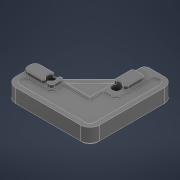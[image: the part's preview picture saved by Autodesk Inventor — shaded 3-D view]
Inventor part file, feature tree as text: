
AUTODESK INVENTOR PART (.ipt)
format: ipt  version: 2022.1 (Build 261234020, 234B)  size: 1,088,512 bytes
history: native  units: mm
features: projected_geometry x18, move_body x16, direct_edit x14, fillet x13, extrude x12, sketch x11, delete_face x9, chamfer x4, plane x1, other x1
ambient origin geometry x8: Origin, YZ Plane, XZ Plane, XY Plane, X Axis, Y Axis, Z Axis, Center Point
bodies: Volumenkörper1 (feature_tree)
feature tree (99):
  direct_edit  "Direktbearbeitung1"
  direct_edit  "Direktbearbeitung2"
  delete_face  "Fläche löschen1"
  extrude  "Extrusion1"  Depth=5.4mm TaperAngle=0.0deg
  fillet  "Rundung1"  Radius=0.5mm
  fillet  "Rundung2"  Radius=6.0mm
  extrude  "Extrusion2"  Depth=1.0mm
  fillet  "Rundung3"  Radius=1.0mm
  extrude  "Extrusion3"  Depth=2.0mm
  delete_face  "Fläche löschen2"
  extrude  "Extrusion4"  Depth=20.0mm
  direct_edit  "Direktbearbeitung3"
  extrude  "Extrusion5"  Depth=1.0mm
  chamfer  "Fase3"  Distance=0.2mm
  plane  "Arbeitsebene1"
  extrude  "Extrusion6"  Depth=0.6mm TaperAngle=0.0deg
  direct_edit  "Direktbearbeitung4"
  direct_edit  "Direktbearbeitung5"
  chamfer  "Fase5"  [1 undecoded]
  direct_edit  "Direktbearbeitung6"
  chamfer  "Fase6"  Distance=1.6mm
  direct_edit  "Direktbearbeitung8"
  delete_face  "Fläche löschen4"
  direct_edit  "Direktbearbeitung9"
  fillet  "Rundung4"  Radius=0.2mm
  fillet  "Rundung5"  Radius=2.0mm
  fillet  "Rundung6"  Radius=16.4mm
  delete_face  "Fläche löschen5"
  delete_face  "Fläche löschen6"
  extrude  "Extrusion7"  Depth=0.6mm
  fillet  "Rundung7"  Radius=0.8mm
  direct_edit  "Direktbearbeitung10"
  sketch  "Skizze8"  dims[d22=1.0mm]
  extrude  "Extrusion8"  Depth=0.6mm
  extrude  "Extrusion9"  Depth=0.6mm
  chamfer  "Fase7"  Distance=0.8mm
  direct_edit  "Direktbearbeitung11"
  extrude  "Extrusion10"  Depth=0.6mm
  fillet  "Rundung8"  Radius=0.4mm
  direct_edit  "Direktbearbeitung12"
  direct_edit  "Direktbearbeitung13"
  fillet  "Rundung9"  Radius=0.4mm
  direct_edit  "Direktbearbeitung14"
  delete_face  "Fläche löschen7"
  delete_face  "Fläche löschen8"
  delete_face  "Fläche löschen9"
  delete_face  "Fläche löschen10"
  direct_edit  "Direktbearbeitung15"
  extrude  "Extrusion11"  Depth=3.0mm
  fillet  "Rundung10"  Radius=3.8mm
  extrude  "Extrusion12"  Depth=0.6mm TaperAngle=0.0deg
  fillet  "Rundung11"  Radius=18.4mm
  fillet  "Rundung12"  Radius=0.6mm
  fillet  "Rundung13"  [1 undecoded]
  sketch  "Skizze1"  dims[d0=0.0mm d1=0.0mm d2=1.4mm d3=0.0mm d4=0.0mm d5=5.4mm d6=0.5mm d7=6.0mm]
  projected_geometry  "Projizierte Kontur1"
  sketch  "Skizze2"  dims[d8=6.0mm d9=0.5mm d10=1.0mm d11=0.0mm]
  projected_geometry  "Projizierte Kontur2"
  projected_geometry  "Projizierte Kontur3"
  sketch  "Skizze3"  dims[d12=0.8mm d13=2.0mm]
  projected_geometry  "Projizierte Kontur4"
  sketch  "Skizze4"  dims[d14=20.0mm d15=20.0mm]
  projected_geometry  "Projizierte Kontur5"
  projected_geometry  "Projizierte Kontur6"
  sketch  "Skizze5"  dims[d16=1.0mm d17=0.0mm d18=1.0mm]
  projected_geometry  "Projizierte Kontur7"
  sketch  "Skizze6"  dims[d20=4.0mm]
  projected_geometry  "Projizierte Kontur8"
  sketch  "Skizze7"  dims[d21=4.0mm]
  projected_geometry  "Projizierte Kontur9"
  projected_geometry  "Projizierte Kontur10"
  projected_geometry  "Projizierte Kontur11"
  projected_geometry  "Projizierte Kontur12"
  projected_geometry  "Projizierte Kontur13"
  sketch  "Skizze9"  dims[d23=1.0mm]
  projected_geometry  "Projizierte Kontur14"
  projected_geometry  "Projizierte Kontur15"
  sketch  "Skizze10"  dims[d24=1.0mm]
  projected_geometry  "Projizierte Kontur16"
  sketch  "Skizze11"  dims[d25=1.0mm d26=0.2mm d27=0.0mm d28=0.2mm d29=0.0mm d30=0.0mm d31=0.0mm d32=-1.6mm d39=1.6mm d40=0.2mm d41=0.0mm d42=0.2mm d43=2.0mm d44=45.0deg d45=16.4mm d46=0.8mm d47=0.8mm d48=7.6mm d49=7.6mm d50=0.8mm d51=0.8mm d52=0.4mm d53=0.4mm d54=3.0mm d55=3.8mm d56=0.6mm d57=0.0mm d58=18.4mm d59=0.0mm d60=0.0mm d61=0.6mm d62=0.0mm d63=0.0mm d64=-0.6mm d68=1.2mm d69=2.0mm d70=45.0deg d71=0.0mm d72=0.0mm d73=-0.2mm d74=0.2mm d75=2.0mm d76=45.0deg d80=0.0mm d81=0.0mm d82=1.9mm d83=0.0mm d84=0.0mm d85=-3.0mm d86=0.0mm d87=0.0mm d88=-3.0mm d89=1.0mm d90=2.0mm d91=1.0mm d92=0.8mm d93=0.8mm d94=4.0mm d95=4.0mm d96=4.0mm d97=4.0mm d98=2.0mm d99=10.0mm d100=0.0mm d101=1.0mm d102=0.0mm d103=0.0mm d104=0.8mm d105=0.0mm d106=0.0mm d107=0.8mm d108=1.6mm d109=4.8mm d111=6.4mm d112=4.8mm d113=6.4mm d114=10.0mm d115=0.0mm d116=10.0mm d117=0.0mm d118=0.2mm d119=2.0mm d120=45.0deg d121=0.0mm d122=0.0mm d123=0.2mm d124=8.0mm d125=0.8mm d126=0.8mm d127=8.0mm d128=10.0mm d129=0.0mm d130=0.8mm d131=0.0mm d132=0.0mm d133=-0.5mm d134=0.0mm d135=0.0mm d136=-0.5mm d137=0.5mm d138=0.0mm d139=0.0mm d140=0.2mm d141=0.0mm d142=-5.0mm d143=0.0mm d144=4.0mm d145=10.0mm d146=0.0mm d147=2.0mm d148=1.0mm d149=0.999999mm d150=1.0mm d151=8.0mm d152=10.0mm d153=0.0mm d154=1.0mm d155=1.0mm d156=0.6mm]
  projected_geometry  "Projizierte Kontur17"
  projected_geometry  "Projizierte Kontur18"
  other  "corner_panel_clip_4mm_x8"
  move_body  "Verschieben1"
  move_body  "Verschieben2"
  move_body  "Verschieben3"
  move_body  "Verschieben4"
  move_body  "Verschieben5"
  move_body  "Verschieben6"
  move_body  "Verschieben8"
  move_body  "Verschieben9"
  move_body  "Verschieben10"
  move_body  "Verschieben11"
  move_body  "Verschieben12"
  move_body  "Verschieben13"
  move_body  "Verschieben14"
  move_body  "Verschieben15"
  move_body  "Verschieben16"
  move_body  "Verschieben17"
note: 2 required parameter values undecoded (feature->parameter linkage not recoverable at this tier; creation-order binding heuristic only, values carry confidence <= 0.55)
